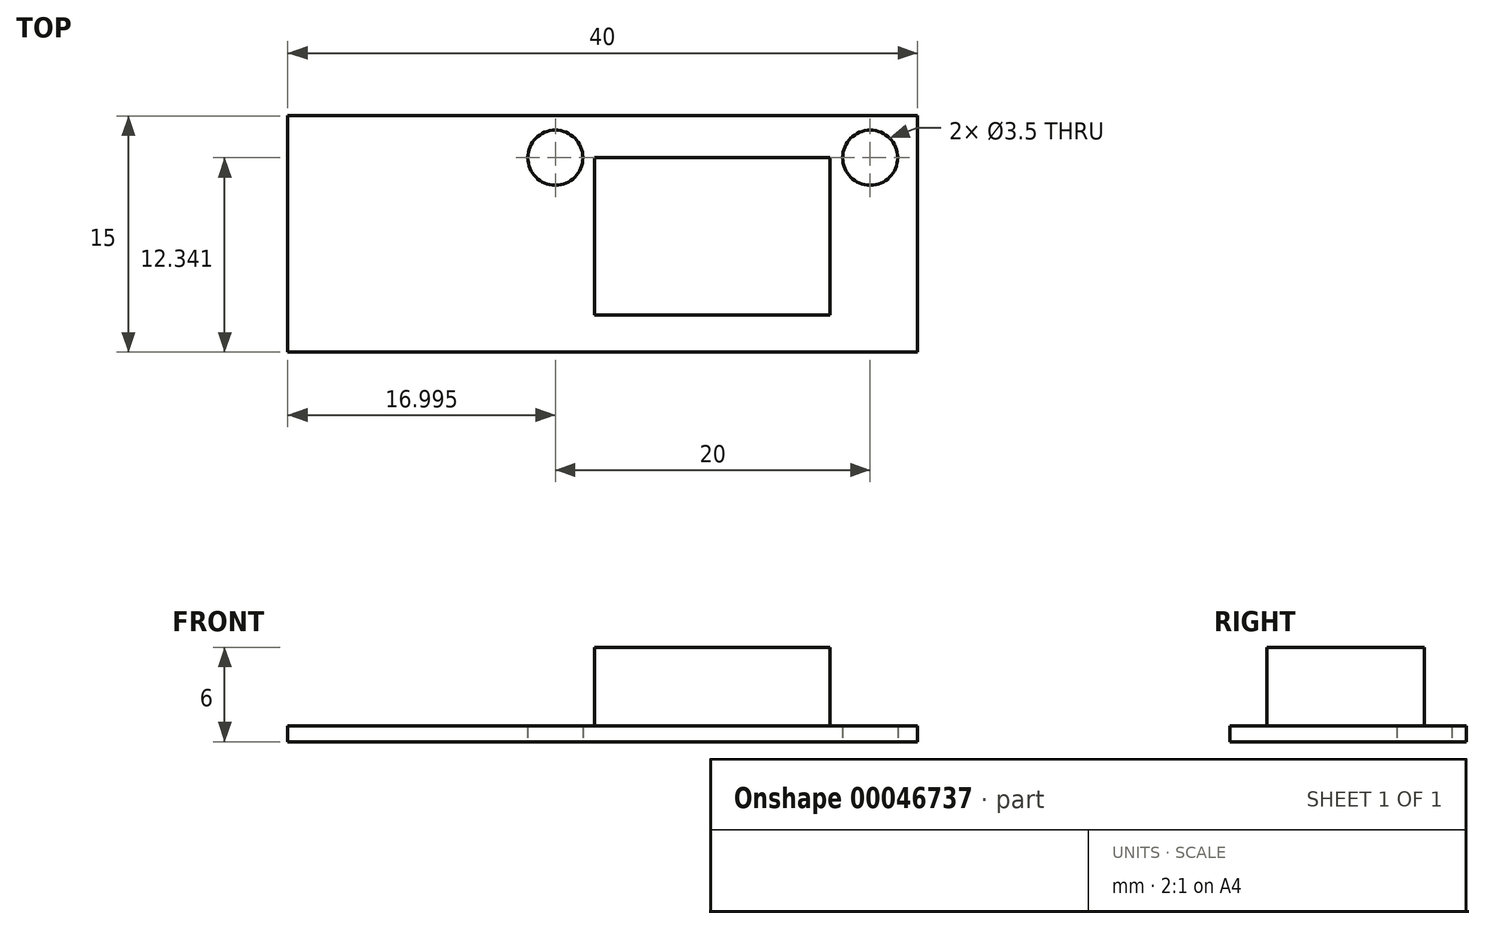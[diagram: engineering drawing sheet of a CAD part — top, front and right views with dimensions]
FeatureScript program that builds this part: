
annotation { "Feature Type Name" : "Feature", "Feature Type Description" : "" }
export const myFeature = defineFeature(function(context is Context, id is Id, definition is map)
    precondition{}
    {
        {
            var Q0;
            Q0=qCreatedBy(makeId("Top.planeOp"),FACE);
            var sketch = newSketch(context, id + "F0", { "sketchPlane" : qUnion([Q0])});
            skLineSegment(sketch, "E0.bottom", {"start": v(-16.63, 5.28) * mm, "end": v(23.37, 5.28) * mm});
            skLineSegment(sketch, "E0.top", {"start": v(-16.63, -9.72) * mm, "end": v(23.37, -9.72) * mm});
            skLineSegment(sketch, "E0.left", {"start": v(-16.63, 5.28) * mm, "end": v(-16.63, -9.72) * mm});
            skLineSegment(sketch, "E0.right", {"start": v(23.37, 5.28) * mm, "end": v(23.37, -9.72) * mm});
            skCircle(sketch, "E1", {"center": v(20.37, 2.62) * mm, "radius": 1.75 * mm});
            skCircle(sketch, "E2", {"center": v(0.37, 2.62) * mm, "radius": 1.75 * mm});
            skSolve(sketch);
        }
        {
            var Q0;
            Q0=qSketchRegion(id+"F0",true);
            extrude(context, id + "F1", {"entities" : qUnion([Q0]), "depth" : 1 * mm});
        }
        {
            var Q0;
            Q0=makeQuery(id+"F1.opExtrude","CAP_FACE",FACE,{"disambiguationData":[OSD([sQuery(id+"F0.wireOp",EDGE,"E0.bottom"),sQuery(id+"F0.wireOp",EDGE,"E0.top"),sQuery(id+"F0.wireOp",EDGE,"E0.left"),sQuery(id+"F0.wireOp",EDGE,"E0.right"),sQuery(id+"F0.wireOp",EDGE,"E1"),sQuery(id+"F0.wireOp",EDGE,"E2")])],"isStart":false});
            var sketch = newSketch(context, id + "F2", { "sketchPlane" : qUnion([Q0])});
            skLineSegment(sketch, "E3.bottom", {"start": v(2.85, 2.65) * mm, "end": v(17.8, 2.65) * mm});
            skLineSegment(sketch, "E3.top", {"start": v(2.85, -7.38) * mm, "end": v(17.8, -7.38) * mm});
            skLineSegment(sketch, "E3.left", {"start": v(2.85, 2.65) * mm, "end": v(2.85, -7.38) * mm});
            skLineSegment(sketch, "E3.right", {"start": v(17.8, 2.65) * mm, "end": v(17.8, -7.38) * mm});
            skSolve(sketch);
        }
        {
            var Q0;
            Q0=qSketchRegion(id+"F2",true);
            extrude(context, id + "F3", {"entities" : qUnion([Q0]), "operationType" : NewBodyOperationType.ADD, "depth" : 5 * mm});
        }
    });
